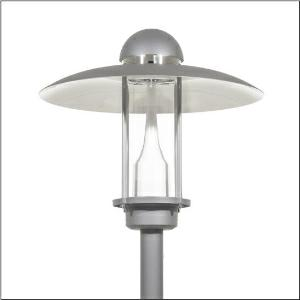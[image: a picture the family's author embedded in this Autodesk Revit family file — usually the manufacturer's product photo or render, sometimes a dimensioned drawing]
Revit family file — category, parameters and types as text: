
# Revit family: city-light_elegance_iq___pl1_2s_5xa5265cf14h_c70b
name_source: partatom
category: Lighting Fixtures
units: mm (PartAtom-declared; Revit-internal decimal feet)

## family parameters
Cut with Voids When Loaded = No
Host = Face
Light Source = No
Part Type = Normal
Room Calculation Point = No
Round Connector Dimension = Use Diameter
Shared = No

## types (1)
- --- (1 x LED, 2840 lm, 23.9 W, 2200K)
    Apparent Load = 24 VA
    CIE Flux Codes = 24 63 94 98 100
    Color Rendering = 70
    Color Temperature = 2200K
    Default Elevation = 1800 mm
    Description = City-Light Elegance iQ, mast luminaire, Module 540 iQ-SR, primary light control with 3 zone facetted reflector, of plastic, silver coated, highly specular, structured, primary optical cover: cover, of PMMA, transparent, light distribution: PL1.2s, light emission: direct distribution, primary light characteristic: symmetric, installation type: post-top, LED, High Power LED, rated luminous flux: 2.840lm, luminous efficacy: 119lm/W, light colour: 722, colour temperature: 2200K, control gear: ECG iQ, control: presetting dimming logarithmic, Street-Remote, Auto-Match, Temp-Guard, Lumen-Switch, Night-Set, Smart-Wire, Light-Fading, Desk-Remote (wireless, voltage-free reading and setting of iQ features in the workshop via application-optimized NFC function/RFID function), optimised constant luminous flux control (CLO 2.0), with terminal, 6-pole, max. 2.5mm², mains connection: 230..240V, AC, 50/60Hz, start of lifetime: 24W, end of service life: 26W, reduction: 12W, luminaire housing, upper part, of aluminium, coated, Siteco® metallic grey (DB 702S), diameter: 750mm, height: 675mm, spigot size: d x l = 76 x 70mm (post-top) | with reducer (optional accessory) 60 x 70mm, post-top mast mounting element, of diecast aluminium, coated, Siteco® metallic grey (DB 702S), Module 540 iQ-SR, traffic white (RAL 9016), equipment: standard, protection rating (complete): IP65, insulation class (complete): insulation class II (safety insulation), certification: CE, ENEC, VDE, packaging unit: 1 piece

Light Distribution: PL1.2s
    Height = 675 mm
    Lamp = 1 x LED
    Lamp Light Flux = 2840 lm
    Lamp Power = 23.9 W
    Lamp count = 1
    Length = 750 mm
    Luminous efficacy = 119 lm/W
    Manufacturer = Siteco
    ModVariant = No
    Model = 5XA5265CF14H
    Number of Poles = 1
    OnlyDefault = Yes
    Power Factor = 1
    Product Name = City-Light Elegance iQ | PL1.2s
    Product group = mast luminaire | pylon top
    ProductGroupID = 6100
    Protection Class = Protection class II
    Protection Degree = IP 65
    RLX_Detail_Level = 1
    RLX_Emergency_Light_Flux = 0 lm
    RLX_Emergency_Type = 0
    RLX_Emergency_Type_DB = No
    RlxData = <blob elided: 72661 chars, md5=5f2bf615>
    Socket = socket
    Standby Power = 0 W
    System Light Flux = 2840 lm
    System Power = 24 W
    Type Comments = factory setting: luminous flux: 100 % | dim-lin: 254 | 499 mA
    Type Image = l_1006912.jpg
    URL = http://relux.com
    VarID = @adj_094979
    Voltage = 0 V
    Weight = 0.00 kg
    Width = 0 mm  [stored 0 ft]

note: [stored X ft] marks values corroborated as IEEE doubles in the binary element streams (Revit-internal decimal feet)

## geometry (parser evidence)
native form markers: Blend x4, Sweep x8
no freeform markers — native parametric forms only
